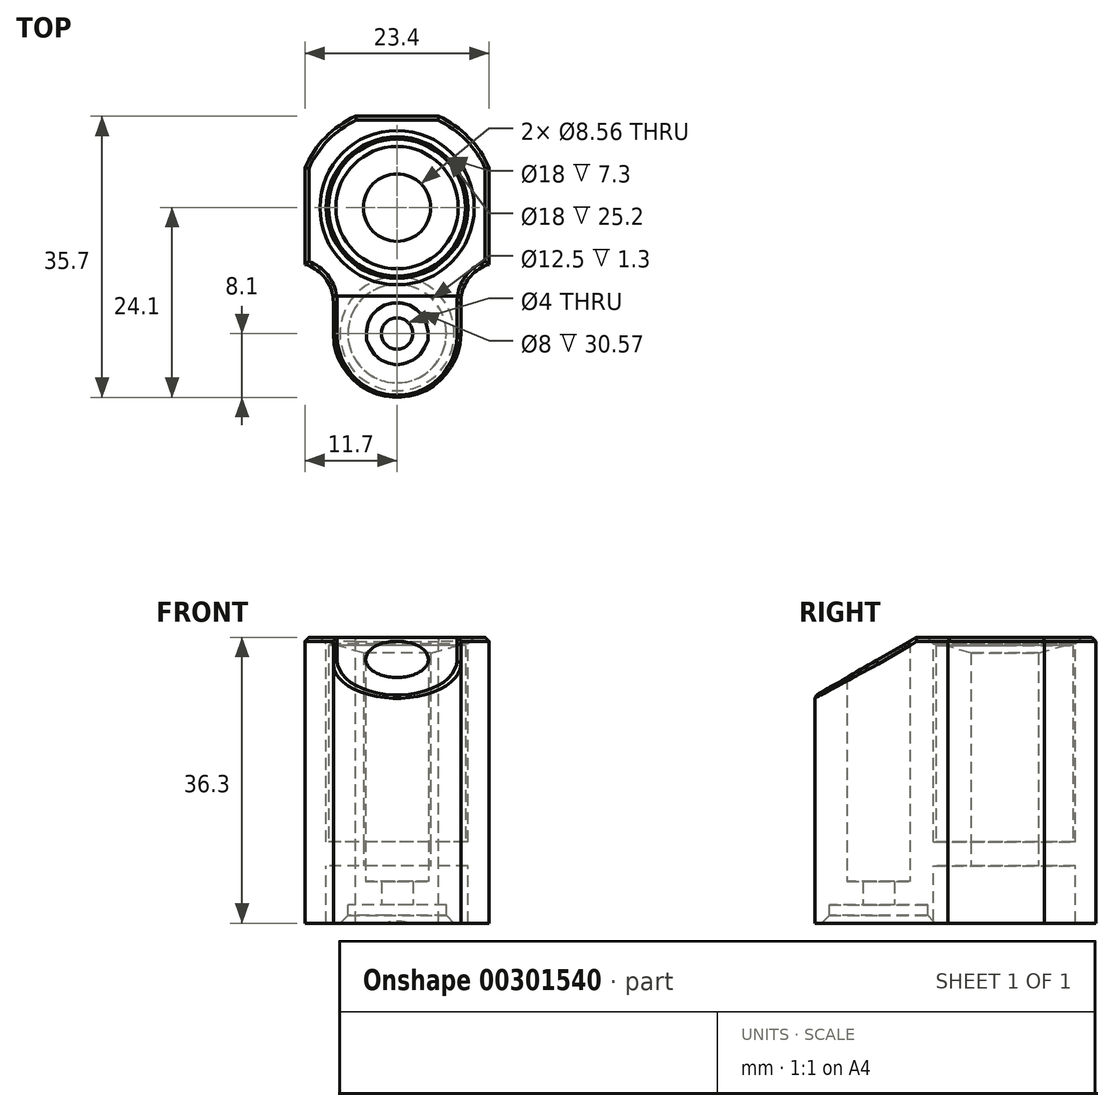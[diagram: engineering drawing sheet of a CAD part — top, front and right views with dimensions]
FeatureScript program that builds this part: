
annotation { "Feature Type Name" : "Feature", "Feature Type Description" : "" }
export const myFeature = defineFeature(function(context is Context, id is Id, definition is map)
    precondition{}
    {
        {
            var Q0;
            Q0=qCreatedBy(makeId("Top.planeOp"),FACE);
            var sketch = newSketch(context, id + "F0", { "sketchPlane" : qUnion([Q0])});
            skCircle(sketch, "E0", {"center": v(0, 0) * mm, "radius": 4.28 * mm});
            skCircle(sketch, "E1", {"center": v(0, 0) * mm, "radius": 9 * mm});
            skCircle(sketch, "E2", {"center": v(0, -16) * mm, "radius": 4 * mm});
            skLineSegment(sketch, "E3", {"start": v(-11.7, 5.07) * mm, "end": v(-11.7, -7.2) * mm});
            skLineSegment(sketch, "E4", {"start": v(11.7, 5.07) * mm, "end": v(11.7, -7.2) * mm});
            skCircle(sketch, "E5", {"center": v(0, 0) * mm, "radius": 12.75 * mm});
            skCircle(sketch, "E6", {"center": v(0, -16) * mm, "radius": 8.1 * mm});
            skLineSegment(sketch, "E7", {"start": v(11.7, -7.2) * mm, "end": v(8.1, -7.2) * mm});
            skLineSegment(sketch, "E8", {"start": v(8.1, -7.2) * mm, "end": v(8.1, -16) * mm});
            skLineSegment(sketch, "E9", {"start": v(-11.7, -7.2) * mm, "end": v(-8.1, -7.2) * mm});
            skLineSegment(sketch, "E10", {"start": v(-8.1, -7.2) * mm, "end": v(-8.1, -16) * mm});
            skLineSegment(sketch, "E11", {"start": v(-5.3, 11.6) * mm, "end": v(5.3, 11.6) * mm});
            skCircle(sketch, "E12", {"center": v(0, -16) * mm, "radius": 2 * mm});
            skCircle(sketch, "E13", {"center": v(0, -16) * mm, "radius": 6.25 * mm});
            skSolve(sketch);
        }
        {
            var Q0;
            {var subQ16=sQuery(id+"F0.wireOp",EDGE,"E11");Q0=makeQuery(id+"F0.imprint","IMPRINT",FACE,{"disambiguationData":[TD([[makeQuery(id+"F0.imprint","IMPRINT",EDGE,{"derivedFrom":subQ16}),-1.0]])]});}
            var Q1;
            {var subQ3=sQuery(id+"F0.wireOp",EDGE,"E6");var subQ5=sQuery(id+"F0.wireOp",EDGE,"E1");var subQ6=makeQuery(id+"F0.imprint","INTERSECT",VERTEX,{"disambiguationData":[OD(0.0)],"derivedFrom":[subQ5,subQ3]});Q1=makeQuery(id+"F0.imprint","IMPRINT",FACE,{"disambiguationData":[TD([[makeQuery(id+"F0.imprint","IMPRINT",EDGE,{"disambiguationData":[TD([[subQ6,1.0]])],"derivedFrom":subQ5}),-1.0]])]});}
            var Q2;
            {var subQ0=sQuery(id+"F0.wireOp",EDGE,"E9");var subQ1=sQuery(id+"F0.wireOp",EDGE,"E3");var subQ2=makeQuery(id+"F0.imprint","INTERSECT",VERTEX,{"derivedFrom":[subQ1,subQ0]});Q2=makeQuery(id+"F0.imprint","IMPRINT",FACE,{"disambiguationData":[TD([[makeQuery(id+"F0.imprint","IMPRINT",EDGE,{"disambiguationData":[TD([[subQ2,1.0]])],"derivedFrom":subQ1}),1.0]])]});}
            var Q3;
            {var subQ0=sQuery(id+"F0.wireOp",EDGE,"E7");var subQ1=sQuery(id+"F0.wireOp",EDGE,"E4");var subQ2=makeQuery(id+"F0.imprint","INTERSECT",VERTEX,{"derivedFrom":[subQ1,subQ0]});Q3=makeQuery(id+"F0.imprint","IMPRINT",FACE,{"disambiguationData":[TD([[makeQuery(id+"F0.imprint","IMPRINT",EDGE,{"disambiguationData":[TD([[subQ2,1.0]])],"derivedFrom":subQ1}),-1.0]])]});}
            var Q4;
            {var subQ0=sQuery(id+"F0.wireOp",EDGE,"E8");var subQ1=sQuery(id+"F0.wireOp",EDGE,"E5");var subQ2=makeQuery(id+"F0.imprint","INTERSECT",VERTEX,{"derivedFrom":[subQ1,subQ0]});Q4=makeQuery(id+"F0.imprint","IMPRINT",FACE,{"disambiguationData":[TD([[makeQuery(id+"F0.imprint","IMPRINT",EDGE,{"disambiguationData":[TD([[subQ2,1.0]])],"derivedFrom":subQ1}),-1.0]])]});}
            var Q5;
            {var subQ0=sQuery(id+"F0.wireOp",EDGE,"E10");var subQ1=sQuery(id+"F0.wireOp",EDGE,"E5");var subQ2=makeQuery(id+"F0.imprint","INTERSECT",VERTEX,{"derivedFrom":[subQ1,subQ0]});Q5=makeQuery(id+"F0.imprint","IMPRINT",FACE,{"disambiguationData":[TD([[makeQuery(id+"F0.imprint","IMPRINT",EDGE,{"disambiguationData":[TD([[subQ2,-1.0]])],"derivedFrom":subQ1}),-1.0]])]});}
            var Q6;
            {var subQ0=sQuery(id+"F0.wireOp",EDGE,"E6");var subQ2=sQuery(id+"F0.wireOp",EDGE,"E5");var subQ3=makeQuery(id+"F0.imprint","INTERSECT",VERTEX,{"disambiguationData":[OD(0.0)],"derivedFrom":[subQ2,subQ0]});Q6=makeQuery(id+"F0.imprint","IMPRINT",FACE,{"disambiguationData":[TD([[makeQuery(id+"F0.imprint","IMPRINT",EDGE,{"disambiguationData":[TD([[subQ3,-1.0]])],"derivedFrom":subQ2}),-1.0]])]});}
            extrude(context, id + "F1", {"entities" : qUnion([Q0, Q1, Q2, Q3, Q4, Q5, Q6]), "oppositeDirection" : true, "depth" : 2.3 * mm});
        }
        {
            var Q0;
            {var subQ0=sQuery(id+"F0.wireOp",EDGE,"E10");var subQ1=sQuery(id+"F0.wireOp",EDGE,"E5");var subQ2=makeQuery(id+"F0.imprint","INTERSECT",VERTEX,{"derivedFrom":[subQ1,subQ0]});Q0=makeQuery(id+"F0.imprint","IMPRINT",FACE,{"disambiguationData":[TD([[makeQuery(id+"F0.imprint","IMPRINT",EDGE,{"disambiguationData":[TD([[subQ2,-1.0]])],"derivedFrom":subQ1}),-1.0]])]});}
            var Q1;
            {var subQ0=sQuery(id+"F0.wireOp",EDGE,"E8");var subQ1=sQuery(id+"F0.wireOp",EDGE,"E5");var subQ2=makeQuery(id+"F0.imprint","INTERSECT",VERTEX,{"derivedFrom":[subQ1,subQ0]});Q1=makeQuery(id+"F0.imprint","IMPRINT",FACE,{"disambiguationData":[TD([[makeQuery(id+"F0.imprint","IMPRINT",EDGE,{"disambiguationData":[TD([[subQ2,1.0]])],"derivedFrom":subQ1}),-1.0]])]});}
            var Q2;
            {var subQ0=sQuery(id+"F0.wireOp",EDGE,"E6");var subQ2=sQuery(id+"F0.wireOp",EDGE,"E5");var subQ3=makeQuery(id+"F0.imprint","INTERSECT",VERTEX,{"disambiguationData":[OD(0.0)],"derivedFrom":[subQ2,subQ0]});Q2=makeQuery(id+"F0.imprint","IMPRINT",FACE,{"disambiguationData":[TD([[makeQuery(id+"F0.imprint","IMPRINT",EDGE,{"disambiguationData":[TD([[subQ3,-1.0]])],"derivedFrom":subQ2}),-1.0]])]});}
            var Q3;
            {var subQ16=sQuery(id+"F0.wireOp",EDGE,"E11");Q3=makeQuery(id+"F0.imprint","IMPRINT",FACE,{"disambiguationData":[TD([[makeQuery(id+"F0.imprint","IMPRINT",EDGE,{"derivedFrom":subQ16}),-1.0]])]});}
            var Q4;
            {var subQ3=sQuery(id+"F0.wireOp",EDGE,"E6");var subQ5=sQuery(id+"F0.wireOp",EDGE,"E1");var subQ6=makeQuery(id+"F0.imprint","INTERSECT",VERTEX,{"disambiguationData":[OD(0.0)],"derivedFrom":[subQ5,subQ3]});Q4=makeQuery(id+"F0.imprint","IMPRINT",FACE,{"disambiguationData":[TD([[makeQuery(id+"F0.imprint","IMPRINT",EDGE,{"disambiguationData":[TD([[subQ6,1.0]])],"derivedFrom":subQ5}),-1.0]])]});}
            var Q5;
            {var subQ0=sQuery(id+"F0.wireOp",EDGE,"E5");var subQ1=sQuery(id+"F0.wireOp",EDGE,"E2");var subQ2=makeQuery(id+"F0.imprint","INTERSECT",VERTEX,{"disambiguationData":[OD(0.0)],"derivedFrom":[subQ1,subQ0]});Q5=makeQuery(id+"F0.imprint","IMPRINT",FACE,{"disambiguationData":[TD([[makeQuery(id+"F0.imprint","IMPRINT",EDGE,{"disambiguationData":[TD([[subQ2,1.0]])],"derivedFrom":subQ1}),-1.0]])]});}
            var Q6;
            {var subQ0=sQuery(id+"F0.wireOp",EDGE,"E5");var subQ1=sQuery(id+"F0.wireOp",EDGE,"E2");var subQ2=makeQuery(id+"F0.imprint","INTERSECT",VERTEX,{"disambiguationData":[OD(0.0)],"derivedFrom":[subQ1,subQ0]});Q6=makeQuery(id+"F0.imprint","IMPRINT",FACE,{"disambiguationData":[TD([[makeQuery(id+"F0.imprint","IMPRINT",EDGE,{"disambiguationData":[TD([[subQ2,-1.0]])],"derivedFrom":subQ1}),-1.0]])]});}
            var Q7;
            Q7=makeQuery(id+"F0.imprint","IMPRINT",FACE,{"disambiguationData":[TD([[makeQuery(id+"F0.imprint","IMPRINT",EDGE,{"derivedFrom":sQuery(id+"F0.wireOp",EDGE,"E12")}),-1.0]])]});
            var Q8;
            {var subQ0=sQuery(id+"F0.wireOp",EDGE,"E5");var subQ1=sQuery(id+"F0.wireOp",EDGE,"E2");var subQ2=makeQuery(id+"F0.imprint","INTERSECT",VERTEX,{"disambiguationData":[OD(0.0)],"derivedFrom":[subQ1,subQ0]});Q8=makeQuery(id+"F0.imprint","IMPRINT",FACE,{"disambiguationData":[TD([[makeQuery(id+"F0.imprint","IMPRINT",EDGE,{"disambiguationData":[TD([[subQ2,1.0]])],"derivedFrom":subQ1}),1.0]])]});}
            var Q9;
            {var subQ0=sQuery(id+"F0.wireOp",EDGE,"E9");var subQ1=sQuery(id+"F0.wireOp",EDGE,"E3");var subQ2=makeQuery(id+"F0.imprint","INTERSECT",VERTEX,{"derivedFrom":[subQ1,subQ0]});Q9=makeQuery(id+"F0.imprint","IMPRINT",FACE,{"disambiguationData":[TD([[makeQuery(id+"F0.imprint","IMPRINT",EDGE,{"disambiguationData":[TD([[subQ2,1.0]])],"derivedFrom":subQ1}),1.0]])]});}
            var Q10;
            {var subQ0=sQuery(id+"F0.wireOp",EDGE,"E7");var subQ1=sQuery(id+"F0.wireOp",EDGE,"E4");var subQ2=makeQuery(id+"F0.imprint","INTERSECT",VERTEX,{"derivedFrom":[subQ1,subQ0]});Q10=makeQuery(id+"F0.imprint","IMPRINT",FACE,{"disambiguationData":[TD([[makeQuery(id+"F0.imprint","IMPRINT",EDGE,{"disambiguationData":[TD([[subQ2,1.0]])],"derivedFrom":subQ1}),-1.0]])]});}
            extrude(context, id + "F2", {"entities" : qUnion([Q0, Q1, Q2, Q3, Q4, Q5, Q6, Q7, Q8, Q9, Q10]), "operationType" : NewBodyOperationType.ADD, "depth" : 3 * mm});
        }
        {
            var Q0;
            {var subQ0=sQuery(id+"F0.wireOp",EDGE,"E9");var subQ1=sQuery(id+"F0.wireOp",EDGE,"E3");var subQ2=makeQuery(id+"F0.imprint","INTERSECT",VERTEX,{"derivedFrom":[subQ1,subQ0]});Q0=makeQuery(id+"F0.imprint","IMPRINT",FACE,{"disambiguationData":[TD([[makeQuery(id+"F0.imprint","IMPRINT",EDGE,{"disambiguationData":[TD([[subQ2,1.0]])],"derivedFrom":subQ1}),1.0]])]});}
            var Q1;
            {var subQ0=sQuery(id+"F0.wireOp",EDGE,"E7");var subQ1=sQuery(id+"F0.wireOp",EDGE,"E4");var subQ2=makeQuery(id+"F0.imprint","INTERSECT",VERTEX,{"derivedFrom":[subQ1,subQ0]});Q1=makeQuery(id+"F0.imprint","IMPRINT",FACE,{"disambiguationData":[TD([[makeQuery(id+"F0.imprint","IMPRINT",EDGE,{"disambiguationData":[TD([[subQ2,1.0]])],"derivedFrom":subQ1}),-1.0]])]});}
            var Q2;
            {var subQ0=sQuery(id+"F0.wireOp",EDGE,"E10");var subQ1=sQuery(id+"F0.wireOp",EDGE,"E5");var subQ2=makeQuery(id+"F0.imprint","INTERSECT",VERTEX,{"derivedFrom":[subQ1,subQ0]});Q2=makeQuery(id+"F0.imprint","IMPRINT",FACE,{"disambiguationData":[TD([[makeQuery(id+"F0.imprint","IMPRINT",EDGE,{"disambiguationData":[TD([[subQ2,-1.0]])],"derivedFrom":subQ1}),-1.0]])]});}
            var Q3;
            {var subQ0=sQuery(id+"F0.wireOp",EDGE,"E8");var subQ1=sQuery(id+"F0.wireOp",EDGE,"E5");var subQ2=makeQuery(id+"F0.imprint","INTERSECT",VERTEX,{"derivedFrom":[subQ1,subQ0]});Q3=makeQuery(id+"F0.imprint","IMPRINT",FACE,{"disambiguationData":[TD([[makeQuery(id+"F0.imprint","IMPRINT",EDGE,{"disambiguationData":[TD([[subQ2,1.0]])],"derivedFrom":subQ1}),-1.0]])]});}
            var Q4;
            {var subQ0=sQuery(id+"F0.wireOp",EDGE,"E6");var subQ2=sQuery(id+"F0.wireOp",EDGE,"E5");var subQ3=makeQuery(id+"F0.imprint","INTERSECT",VERTEX,{"disambiguationData":[OD(0.0)],"derivedFrom":[subQ2,subQ0]});Q4=makeQuery(id+"F0.imprint","IMPRINT",FACE,{"disambiguationData":[TD([[makeQuery(id+"F0.imprint","IMPRINT",EDGE,{"disambiguationData":[TD([[subQ3,-1.0]])],"derivedFrom":subQ2}),-1.0]])]});}
            var Q5;
            {var subQ16=sQuery(id+"F0.wireOp",EDGE,"E11");Q5=makeQuery(id+"F0.imprint","IMPRINT",FACE,{"disambiguationData":[TD([[makeQuery(id+"F0.imprint","IMPRINT",EDGE,{"derivedFrom":subQ16}),-1.0]])]});}
            var Q6;
            {var subQ3=sQuery(id+"F0.wireOp",EDGE,"E6");var subQ5=sQuery(id+"F0.wireOp",EDGE,"E1");var subQ6=makeQuery(id+"F0.imprint","INTERSECT",VERTEX,{"disambiguationData":[OD(0.0)],"derivedFrom":[subQ5,subQ3]});Q6=makeQuery(id+"F0.imprint","IMPRINT",FACE,{"disambiguationData":[TD([[makeQuery(id+"F0.imprint","IMPRINT",EDGE,{"disambiguationData":[TD([[subQ6,1.0]])],"derivedFrom":subQ5}),-1.0]])]});}
            var Q7;
            {var subQ0=sQuery(id+"F0.wireOp",EDGE,"E5");var subQ1=sQuery(id+"F0.wireOp",EDGE,"E2");var subQ2=makeQuery(id+"F0.imprint","INTERSECT",VERTEX,{"disambiguationData":[OD(0.0)],"derivedFrom":[subQ1,subQ0]});Q7=makeQuery(id+"F0.imprint","IMPRINT",FACE,{"disambiguationData":[TD([[makeQuery(id+"F0.imprint","IMPRINT",EDGE,{"disambiguationData":[TD([[subQ2,1.0]])],"derivedFrom":subQ1}),-1.0]])]});}
            var Q8;
            {var subQ0=sQuery(id+"F0.wireOp",EDGE,"E5");var subQ1=sQuery(id+"F0.wireOp",EDGE,"E2");var subQ2=makeQuery(id+"F0.imprint","INTERSECT",VERTEX,{"disambiguationData":[OD(0.0)],"derivedFrom":[subQ1,subQ0]});Q8=makeQuery(id+"F0.imprint","IMPRINT",FACE,{"disambiguationData":[TD([[makeQuery(id+"F0.imprint","IMPRINT",EDGE,{"disambiguationData":[TD([[subQ2,-1.0]])],"derivedFrom":subQ1}),-1.0]])]});}
            extrude(context, id + "F3", {"entities" : qUnion([Q0, Q1, Q2, Q3, Q4, Q5, Q6, Q7, Q8]), "operationType" : NewBodyOperationType.ADD, "depth" : 34 * mm, "hasSecondDirection" : true, "secondDirectionOppositeDirection" : false, "secondDirectionDepth" : 3 * mm});
        }
        {
            var Q0;
            {var subQ0=sQuery(id+"F0.wireOp",EDGE,"E10");var subQ1=sQuery(id+"F0.wireOp",EDGE,"E9");Q0=makeQuery(id+"F3.boolean.opBoolean","MERGE",EDGE,{"derivedFrom":[makeQuery(id+"F2.boolean.opBoolean","MERGE",EDGE,{"derivedFrom":[makeQuery(id+"F1.opExtrude","SWEPT_EDGE",EDGE,{"disambiguationData":[OSD([subQ1,subQ0])]}),makeQuery(id+"F2.opExtrude","SWEPT_EDGE",EDGE,{"disambiguationData":[OSD([subQ1,subQ0])]})]}),makeQuery(id+"F3.opExtrude","SWEPT_EDGE",EDGE,{"disambiguationData":[OSD([subQ1,subQ0])]})]});}
            var Q1;
            {var subQ0=sQuery(id+"F0.wireOp",EDGE,"E8");var subQ1=sQuery(id+"F0.wireOp",EDGE,"E7");Q1=makeQuery(id+"F3.boolean.opBoolean","MERGE",EDGE,{"derivedFrom":[makeQuery(id+"F2.boolean.opBoolean","MERGE",EDGE,{"derivedFrom":[makeQuery(id+"F1.opExtrude","SWEPT_EDGE",EDGE,{"disambiguationData":[OSD([subQ1,subQ0])]}),makeQuery(id+"F2.opExtrude","SWEPT_EDGE",EDGE,{"disambiguationData":[OSD([subQ1,subQ0])]})]}),makeQuery(id+"F3.opExtrude","SWEPT_EDGE",EDGE,{"disambiguationData":[OSD([subQ1,subQ0])]})]});}
            fillet(context, id + "F4", {"entities" : qUnion([Q0, Q1]), "radius" : 5 * mm, "tangentPropagation" : true, "allowEdgeOverflow" : false});
        }
        {
            var Q0;
            Q0=qCreatedBy(makeId("Right.planeOp"),FACE);
            var sketch = newSketch(context, id + "F5", { "sketchPlane" : qUnion([Q0])});
            skLineSegment(sketch, "E14", {"start": v(-11.2, 34) * mm, "end": v(-7.2, 34) * mm});
            skLineSegment(sketch, "E15", {"start": v(-11.2, 34) * mm, "end": v(-31.2, 22.45) * mm});
            skLineSegment(sketch, "E16", {"start": v(-31.2, 22.45) * mm, "end": v(-31.2, 34) * mm});
            skLineSegment(sketch, "E17", {"start": v(-31.2, 34) * mm, "end": v(-11.2, 34) * mm});
            skSolve(sketch);
        }
        {
            var Q0;
            Q0 = qSketchRegion(id + "F5", true);
            extrude(context, id + "F6", {"entities" : qUnion([Q0]), "operationType" : NewBodyOperationType.REMOVE, "endBound" : BoundingType.SYMMETRIC, "depth" : 25 * mm});
        }
        {
            var Q0;
            Q0=qCreatedBy(makeId("Right.planeOp"),FACE);
            var sketch = newSketch(context, id + "F7", { "sketchPlane" : qUnion([Q0])});
            skLineSegment(sketch, "E18.bottom", {"start": v(11.6, 29) * mm, "end": v(10.6, 29) * mm});
            skLineSegment(sketch, "E18.top", {"start": v(11.6, 17) * mm, "end": v(10.6, 17) * mm});
            skLineSegment(sketch, "E18.left", {"start": v(11.6, 29) * mm, "end": v(11.6, 17) * mm});
            skLineSegment(sketch, "E18.right", {"start": v(7.6, 26) * mm, "end": v(7.6, 20) * mm});
            skPoint(sketch, "E19.visualSharp", {"position": v(7.6, 29) * mm});
            skArc(sketch, "E19.filletArc", {"start": v(10.6, 29) * mm, "mid": v(8.48, 28.12) * mm, "end": v(7.6, 26) * mm});
            skPoint(sketch, "E20.visualSharp", {"position": v(7.6, 17) * mm});
            skArc(sketch, "E20.filletArc", {"start": v(7.6, 20) * mm, "mid": v(8.48, 17.88) * mm, "end": v(10.6, 17) * mm});
            skSolve(sketch);
        }
        {
            var Q0;
            Q0=makeQuery(id+"F0.imprint","IMPRINT",FACE,{"disambiguationData":[TD([[makeQuery(id+"F0.imprint","IMPRINT",EDGE,{"derivedFrom":sQuery(id+"F0.wireOp",EDGE,"E0")}),-1.0]])]});
            var Q1;
            {var subQ0=sQuery(id+"F0.wireOp",EDGE,"E6");var subQ1=sQuery(id+"F0.wireOp",EDGE,"E1");var subQ2=makeQuery(id+"F0.imprint","INTERSECT",VERTEX,{"disambiguationData":[OD(0.0)],"derivedFrom":[subQ1,subQ0]});Q1=makeQuery(id+"F0.imprint","IMPRINT",FACE,{"disambiguationData":[TD([[makeQuery(id+"F0.imprint","IMPRINT",EDGE,{"disambiguationData":[TD([[subQ2,1.0]])],"derivedFrom":subQ1}),1.0]])]});}
            extrude(context, id + "F8", {"entities" : qUnion([Q0, Q1]), "operationType" : NewBodyOperationType.ADD, "depth" : 8 * mm, "hasSecondDirection" : true, "secondDirectionOppositeDirection" : false, "secondDirectionDepth" : 5 * mm});
        }
        {
            var Q0;
            Q0=makeQuery(id+"F1.opExtrude","CAP_EDGE",EDGE,{"disambiguationData":[OSD([sQuery(id+"F0.wireOp",EDGE,"E13")])],"isStart":false});
            chamfer(context, id + "F9", {"entities" : qUnion([Q0]), "width" : 1 * mm, "tangentPropagation" : true});
        }
        {
            var Q0;
            Q0=makeQuery(id+"F8.opExtrude","CAP_FACE",FACE,{"disambiguationData":[OSD([sQuery(id+"F0.wireOp",EDGE,"E0"),sQuery(id+"F0.wireOp",EDGE,"E1")])],"isStart":false});
            cPlane(context, id + "F10", {"entities" : qUnion([Q0]), "cplaneType" : CPlaneType.OFFSET, "offset" : 0 * mm, "width" : 150 * mm, "height" : 150 * mm});
        }
        {
            var Q0;
            Q0=qCreatedBy(id+"F10.planeOp",FACE);
            var sketch = newSketch(context, id + "F11", { "sketchPlane" : qUnion([Q0])});
            skCircle(sketch, "E21", {"center": v(0, 0) * mm, "radius": 4.28 * mm});
            skCircle(sketch, "E22", {"center": v(0, 0) * mm, "radius": 8.7 * mm});
            skSolve(sketch);
        }
        {
            var Q0;
            Q0 = qSketchRegion(id + "F11", true);
            var Q1;
            Q1=makeQuery(id+"F11.imprint","IMPRINT",FACE,{"disambiguationData":[TD([[makeQuery(id+"F11.imprint","IMPRINT",EDGE,{"derivedFrom":sQuery(id+"F11.wireOp",EDGE,"E21")}),-1.0]])]});
            extrude(context, id + "F12", {"entities" : qUnion([Q0, Q1]), "depth" : 25 * mm});
        }
        {
            var Q0;
            Q0=makeQuery(id+"F12.opExtrude","CAP_EDGE",EDGE,{"disambiguationData":[OSD([sQuery(id+"F11.wireOp",EDGE,"E21")])],"isStart":false});
            chamfer(context, id + "F13", {"entities" : qUnion([Q0]), "chamferType" : ChamferType.OFFSET_ANGLE, "width" : 1 * mm, "oppositeDirection" : false, "angle" : 74 * degree});
        }
        {
            var Q0;
            {var subQ0=sQuery(id+"F0.wireOp",EDGE,"E8");Q0=makeQuery(id+"F6.boolean.opBoolean","INTERSECT",EDGE,{"derivedFrom":[makeQuery(id+"F3.boolean.opBoolean","MERGE",FACE,{"derivedFrom":[makeQuery(id+"F2.boolean.opBoolean","MERGE",FACE,{"derivedFrom":[makeQuery(id+"F1.opExtrude","SWEPT_FACE",FACE,{"disambiguationData":[OSD([subQ0])]}),makeQuery(id+"F2.opExtrude","SWEPT_FACE",FACE,{"disambiguationData":[OSD([subQ0])]})]}),makeQuery(id+"F3.opExtrude","SWEPT_FACE",FACE,{"disambiguationData":[OSD([subQ0])]})]}),makeQuery(id+"F6.opExtrude","SWEPT_FACE",FACE,{"disambiguationData":[OSD([sQuery(id+"F5.wireOp",EDGE,"E15")])]})]});}
            var Q1;
            Q1=makeQuery(id+"F3.opExtrude","CAP_EDGE",EDGE,{"disambiguationData":[OSD([sQuery(id+"F0.wireOp",EDGE,"E4")])],"isStart":false});
            var Q2;
            {var subQ0=sQuery(id+"F0.wireOp",EDGE,"E5");Q2=makeQuery(id+"F3.opExtrude","CAP_EDGE",EDGE,{"disambiguationData":[OSD([subQ0]),TDD([makeQuery(id+"F0.imprint","IMPRINT",EDGE,{"disambiguationData":[TD([[makeQuery(id+"F0.imprint","INTERSECT",VERTEX,{"disambiguationData":[OD(0.0)],"derivedFrom":[sQuery(id+"F0.wireOp",EDGE,"E4"),subQ0]}),-1.0]])],"derivedFrom":subQ0})])],"isStart":false});}
            var Q3;
            Q3=makeQuery(id+"F3.opExtrude","CAP_EDGE",EDGE,{"disambiguationData":[OSD([sQuery(id+"F0.wireOp",EDGE,"E11")])],"isStart":false});
            var Q4;
            {var subQ0=sQuery(id+"F0.wireOp",EDGE,"E5");Q4=makeQuery(id+"F3.opExtrude","CAP_EDGE",EDGE,{"disambiguationData":[OSD([subQ0]),TDD([makeQuery(id+"F0.imprint","IMPRINT",EDGE,{"disambiguationData":[TD([[makeQuery(id+"F0.imprint","INTERSECT",VERTEX,{"disambiguationData":[OD(0.0)],"derivedFrom":[sQuery(id+"F0.wireOp",EDGE,"E3"),subQ0]}),1.0]])],"derivedFrom":subQ0})])],"isStart":false});}
            var Q5;
            Q5=makeQuery(id+"F3.opExtrude","CAP_EDGE",EDGE,{"disambiguationData":[OSD([sQuery(id+"F0.wireOp",EDGE,"E3")])],"isStart":false});
            var Q6;
            {var subQ0=sQuery(id+"F0.wireOp",EDGE,"E8");var subQ1=sQuery(id+"F0.wireOp",EDGE,"E7");Q6=makeQuery(id+"F4.opFillet","BLEND_EDGE",EDGE,{"blendedFrom":[makeQuery(id+"F3.boolean.opBoolean","MERGE",EDGE,{"derivedFrom":[makeQuery(id+"F2.boolean.opBoolean","MERGE",EDGE,{"derivedFrom":[makeQuery(id+"F1.opExtrude","SWEPT_EDGE",EDGE,{"disambiguationData":[OSD([subQ1,subQ0])]}),makeQuery(id+"F2.opExtrude","SWEPT_EDGE",EDGE,{"disambiguationData":[OSD([subQ1,subQ0])]})]}),makeQuery(id+"F3.opExtrude","SWEPT_EDGE",EDGE,{"disambiguationData":[OSD([subQ1,subQ0])]})]}),makeQuery(id+"F3.opExtrude","CAP_FACE",FACE,{"disambiguationData":[OSD([sQuery(id+"F0.wireOp",EDGE,"E1"),sQuery(id+"F0.wireOp",EDGE,"E2"),sQuery(id+"F0.wireOp",EDGE,"E3"),sQuery(id+"F0.wireOp",EDGE,"E4"),sQuery(id+"F0.wireOp",EDGE,"E5"),sQuery(id+"F0.wireOp",EDGE,"E6"),subQ1,subQ0,sQuery(id+"F0.wireOp",EDGE,"E9"),sQuery(id+"F0.wireOp",EDGE,"E10"),sQuery(id+"F0.wireOp",EDGE,"E11")])],"isStart":false})],"blendedInto":[makeQuery(id+"F3.opExtrude","CAP_FACE",FACE,{"disambiguationData":[OSD([sQuery(id+"F0.wireOp",EDGE,"E1"),sQuery(id+"F0.wireOp",EDGE,"E2"),sQuery(id+"F0.wireOp",EDGE,"E3"),sQuery(id+"F0.wireOp",EDGE,"E4"),sQuery(id+"F0.wireOp",EDGE,"E5"),sQuery(id+"F0.wireOp",EDGE,"E6"),subQ1,subQ0,sQuery(id+"F0.wireOp",EDGE,"E9"),sQuery(id+"F0.wireOp",EDGE,"E10"),sQuery(id+"F0.wireOp",EDGE,"E11")])],"isStart":false})]});}
            var Q7;
            {var subQ0=sQuery(id+"F0.wireOp",EDGE,"E10");var subQ1=sQuery(id+"F0.wireOp",EDGE,"E9");Q7=makeQuery(id+"F4.opFillet","BLEND_EDGE",EDGE,{"blendedFrom":[makeQuery(id+"F3.boolean.opBoolean","MERGE",EDGE,{"derivedFrom":[makeQuery(id+"F2.boolean.opBoolean","MERGE",EDGE,{"derivedFrom":[makeQuery(id+"F1.opExtrude","SWEPT_EDGE",EDGE,{"disambiguationData":[OSD([subQ1,subQ0])]}),makeQuery(id+"F2.opExtrude","SWEPT_EDGE",EDGE,{"disambiguationData":[OSD([subQ1,subQ0])]})]}),makeQuery(id+"F3.opExtrude","SWEPT_EDGE",EDGE,{"disambiguationData":[OSD([subQ1,subQ0])]})]}),makeQuery(id+"F3.opExtrude","CAP_FACE",FACE,{"disambiguationData":[OSD([sQuery(id+"F0.wireOp",EDGE,"E1"),sQuery(id+"F0.wireOp",EDGE,"E2"),sQuery(id+"F0.wireOp",EDGE,"E3"),sQuery(id+"F0.wireOp",EDGE,"E4"),sQuery(id+"F0.wireOp",EDGE,"E5"),sQuery(id+"F0.wireOp",EDGE,"E6"),sQuery(id+"F0.wireOp",EDGE,"E7"),sQuery(id+"F0.wireOp",EDGE,"E8"),subQ1,subQ0,sQuery(id+"F0.wireOp",EDGE,"E11")])],"isStart":false})],"blendedInto":[makeQuery(id+"F3.opExtrude","CAP_FACE",FACE,{"disambiguationData":[OSD([sQuery(id+"F0.wireOp",EDGE,"E1"),sQuery(id+"F0.wireOp",EDGE,"E2"),sQuery(id+"F0.wireOp",EDGE,"E3"),sQuery(id+"F0.wireOp",EDGE,"E4"),sQuery(id+"F0.wireOp",EDGE,"E5"),sQuery(id+"F0.wireOp",EDGE,"E6"),sQuery(id+"F0.wireOp",EDGE,"E7"),sQuery(id+"F0.wireOp",EDGE,"E8"),subQ1,subQ0,sQuery(id+"F0.wireOp",EDGE,"E11")])],"isStart":false})]});}
            chamfer(context, id + "F14", {"entities" : qUnion([Q0, Q1, Q2, Q3, Q4, Q5, Q6, Q7]), "width" : 0.5 * mm, "tangentPropagation" : true});
        }
        {
            var Q0;
            Q0=makeQuery(id+"F3.opExtrude","CAP_EDGE",EDGE,{"disambiguationData":[OSD([sQuery(id+"F0.wireOp",EDGE,"E1")])],"isStart":false});
            chamfer(context, id + "F15", {"entities" : qUnion([Q0]), "width" : 0.8 * mm, "tangentPropagation" : true});
        }
    });
